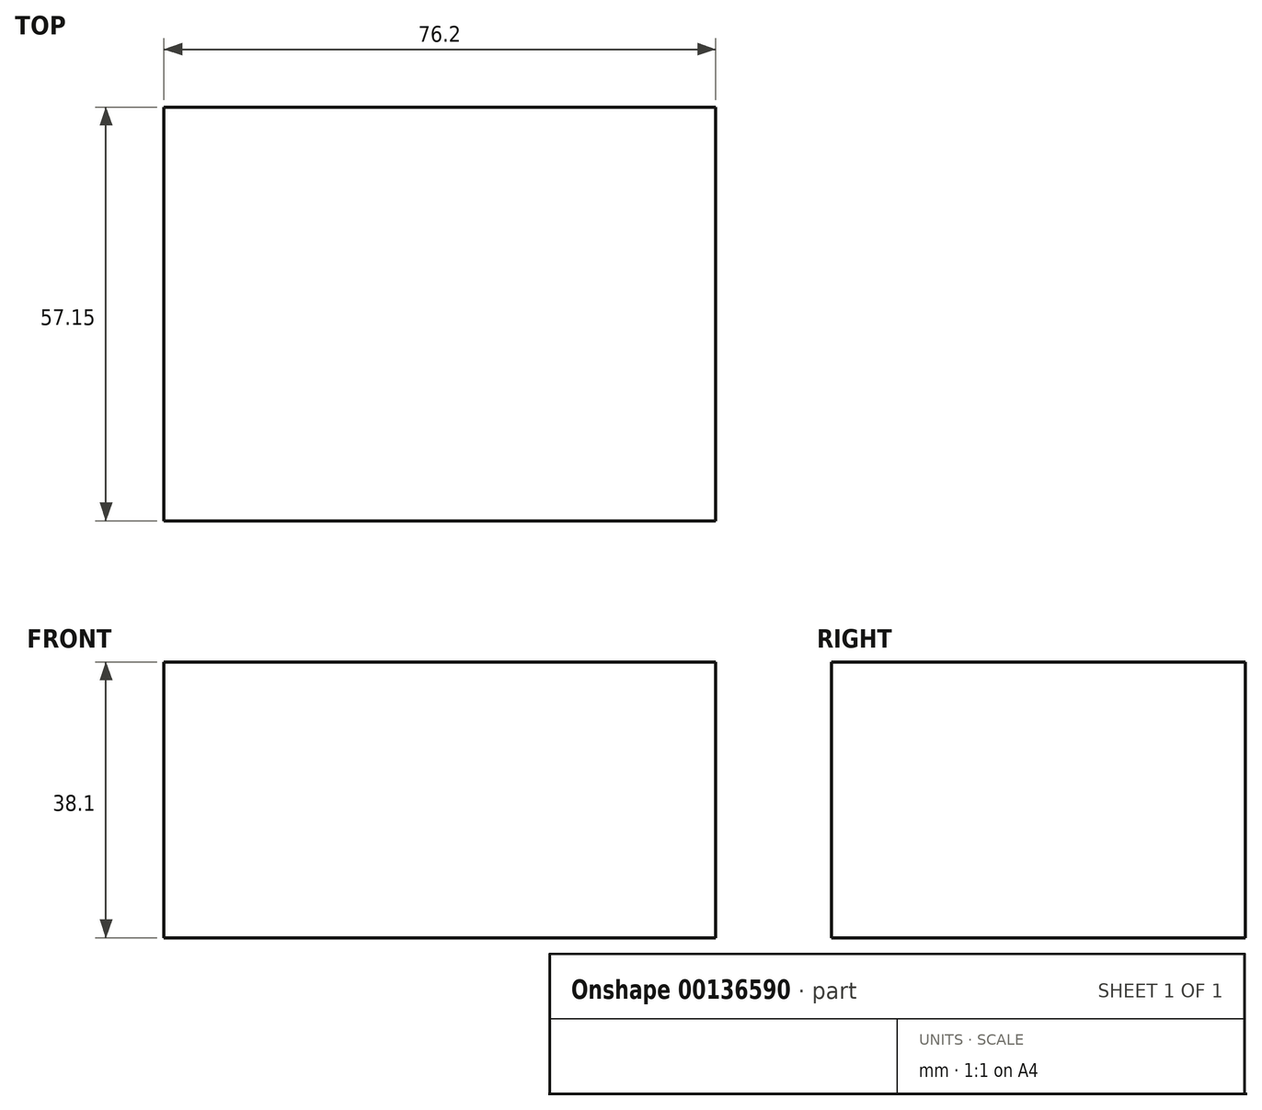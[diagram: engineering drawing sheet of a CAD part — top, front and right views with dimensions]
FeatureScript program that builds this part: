
annotation { "Feature Type Name" : "Feature", "Feature Type Description" : "" }
export const myFeature = defineFeature(function(context is Context, id is Id, definition is map)
    precondition{}
    {
        {
            var Q0;
            Q0=qCreatedBy(makeId("Front.planeOp"),FACE);
            var sketch = newSketch(context, id + "F0", { "sketchPlane" : qUnion([Q0])});
            skLineSegment(sketch, "E0.bottom", {"start": v(3.11, 0) * mm, "end": v(79.31, 0) * mm});
            skLineSegment(sketch, "E0.top", {"start": v(3.11, 38.1) * mm, "end": v(79.31, 38.1) * mm});
            skLineSegment(sketch, "E0.left", {"start": v(3.11, 0) * mm, "end": v(3.11, 38.1) * mm});
            skLineSegment(sketch, "E0.right", {"start": v(79.31, 0) * mm, "end": v(79.31, 38.1) * mm});
            skSolve(sketch);
        }
        {
            var Q0;
            Q0=makeQuery(id+"F0.imprint","IMPRINT",FACE,{"disambiguationData":[TD([[makeQuery(id+"F0.imprint","IMPRINT",EDGE,{"derivedFrom":sQuery(id+"F0.wireOp",EDGE,"E0.bottom")}),1.0]])]});
            extrude(context, id + "F1", {"entities" : qUnion([Q0]), "depth" : 57.15 * mm});
        }
    });
